# Revit family: 2Incepa_Ocean_Cuba de Apoio Pacific_63067
name_source: partatom
category: Plumbing Fixtures
revit_build: Autodesk Revit MEP 2014 (Build: 20131024_2115(x64)
units: mm (PartAtom-declared; Revit-internal decimal feet)

## types (1)
- 01 - Branco
    Assembly Code = D2010400
    CWFU = 0
    Default Elevation = 0 mm  [stored 0 ft]
    Description = Cuba de apoio Pacific cor branca (63067), 500 x 410 mm, linha Ocean - Louças Incepa
    Desenvolvido por = ofcdesk
    Diâmetro Ponto de Esgoto = 40 mm
    HWFU = 0
    Incepa: Categoria = Cubas e Lavatórios
    Incepa: Cores Disponíveis = Branco
    Incepa: Código = 63067
    Incepa: Descrição = Cuba de apoio Pacific cor branca (63067), 500 x 410 mm, linha Ocean - Louças Incepa
    Incepa: Fabricante = Incepa
    Incepa: Linha = Ocean
    Incepa: Link do Produto = http://www.banheirosincepa.com.br
    Incepa: Norma = ABNT NBR 15097-1: 2011 - Requisitos e métodos de ensaio
    Incepa: Produto = Louças
    Incepa: Tipo = Cubas
    Incepa: Versão = Autodesk Revit MEP 2014
    Manufacturer = Incepa
    Model = 63067
    Raio Ponto de Esgoto = 20 mm
    Selo de Qualidade ofcdesk = Standard
    URL = http://www.banheirosincepa.com.br
    WFU = 2

note: [stored X ft] marks values corroborated as IEEE doubles in the binary element streams (Revit-internal decimal feet)

## geometry (parser evidence)
native form markers: Blend x4, Sweep x10
no freeform markers — native parametric forms only
